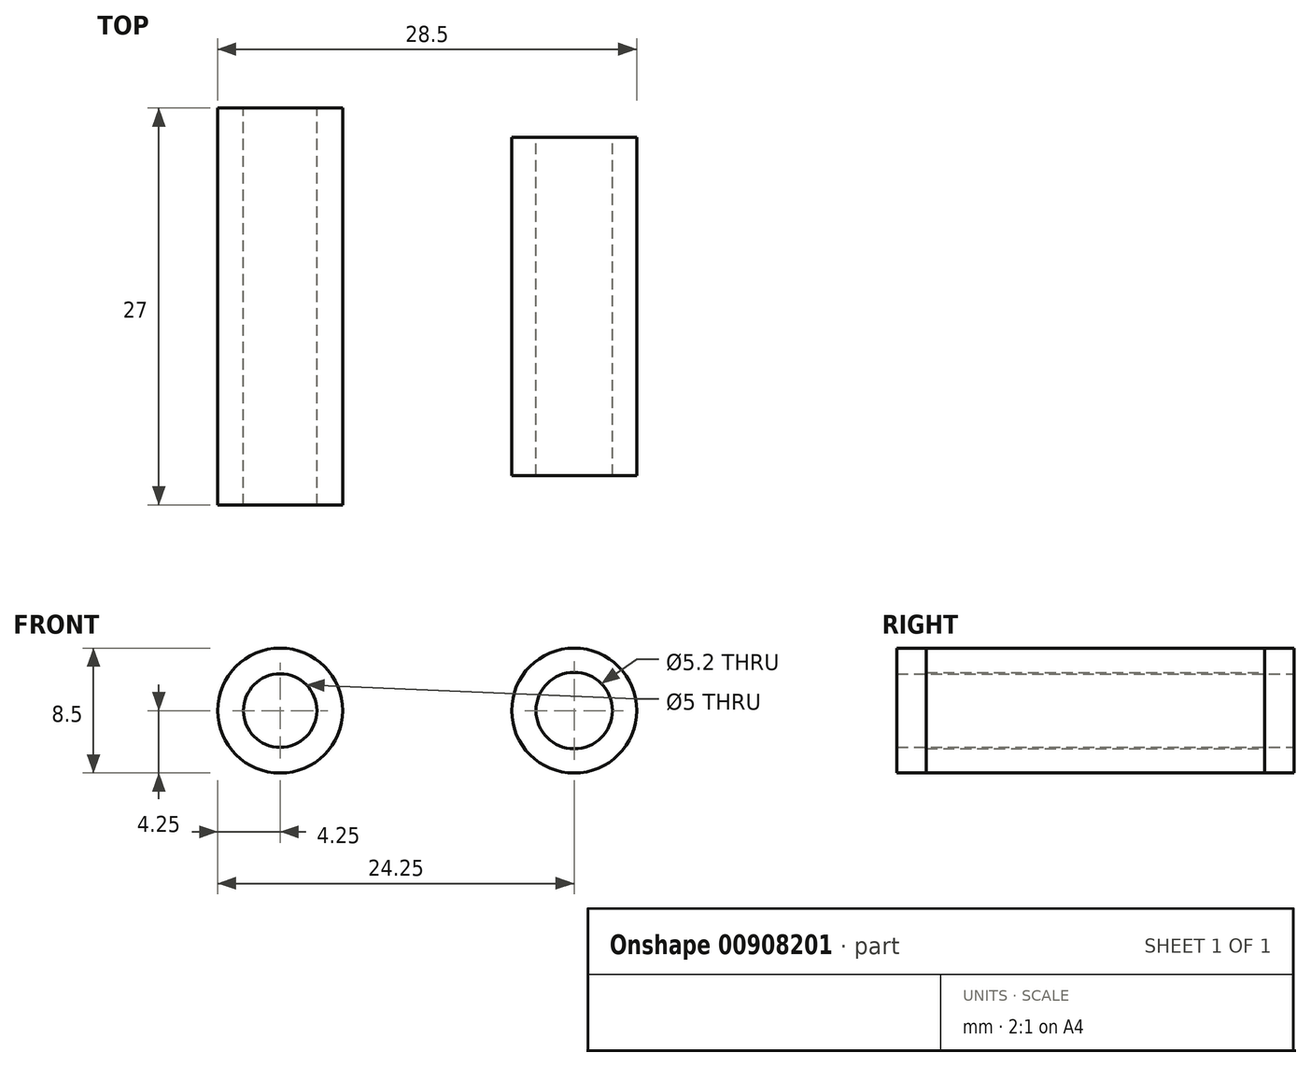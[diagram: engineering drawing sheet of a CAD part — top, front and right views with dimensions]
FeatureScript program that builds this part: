
annotation { "Feature Type Name" : "Feature", "Feature Type Description" : "" }
export const myFeature = defineFeature(function(context is Context, id is Id, definition is map)
    precondition{}
    {
        {
            var Q0;
            Q0=qCreatedBy(makeId("Front.planeOp"),FACE);
            var sketch = newSketch(context, id + "F0", { "sketchPlane" : qUnion([Q0])});
            skCircle(sketch, "E0", {"center": v(0, 0) * mm, "radius": 4.25 * mm});
            skCircle(sketch, "E1", {"center": v(0, 0) * mm, "radius": 2.5 * mm});
            skSolve(sketch);
        }
        {
            var Q0;
            Q0 = qSketchRegion(id + "F0", true);
            extrude(context, id + "F1", {"entities" : qUnion([Q0]), "depth" : 27 * mm, "offsetDistance" : 25 * mm, "symmetric" : true});
        }
        {
            var Q0;
            Q0=qCreatedBy(makeId("Front.planeOp"),FACE);
            var sketch = newSketch(context, id + "F2", { "sketchPlane" : qUnion([Q0])});
            skCircle(sketch, "E2", {"center": v(20, 0) * mm, "radius": 4.25 * mm});
            skCircle(sketch, "E3", {"center": v(20, 0) * mm, "radius": 2.6 * mm});
            skLineSegment(sketch, "E4", {"start": v(0, 0) * mm, "end": v(20, 0) * mm, "construction": true});
            skSolve(sketch);
        }
        {
            var Q0;
            Q0 = qSketchRegion(id + "F2", true);
            var Q1;
            Q1=makeQuery(id+"F1.opExtrude","CAP_FACE",FACE,{"disambiguationData":[OSD([sQuery(id+"F0.wireOp",EDGE,"E0"),sQuery(id+"F0.wireOp",EDGE,"E1")])],"isStart":false});
            var Q2;
            Q2=makeQuery(id+"F1.opExtrude","CAP_FACE",FACE,{"disambiguationData":[OSD([sQuery(id+"F0.wireOp",EDGE,"E0"),sQuery(id+"F0.wireOp",EDGE,"E1")])],"isStart":true});
            extrude(context, id + "F3", {"entities" : qUnion([Q0]), "endBound" : BoundingType.UP_TO_SURFACE, "depth" : 25 * mm, "endBoundEntityFace" : qUnion([Q1]), "hasOffset" : true, "offsetDistance" : 2 * mm, "hasSecondDirection" : true, "secondDirectionBound" : BoundingType.UP_TO_SURFACE, "secondDirectionOppositeDirection" : true, "secondDirectionDepth" : 25 * mm, "secondDirectionBoundEntityFace" : qUnion([Q2]), "hasSecondDirectionOffset" : true, "secondDirectionOffsetDistance" : 2 * mm});
        }
    });
